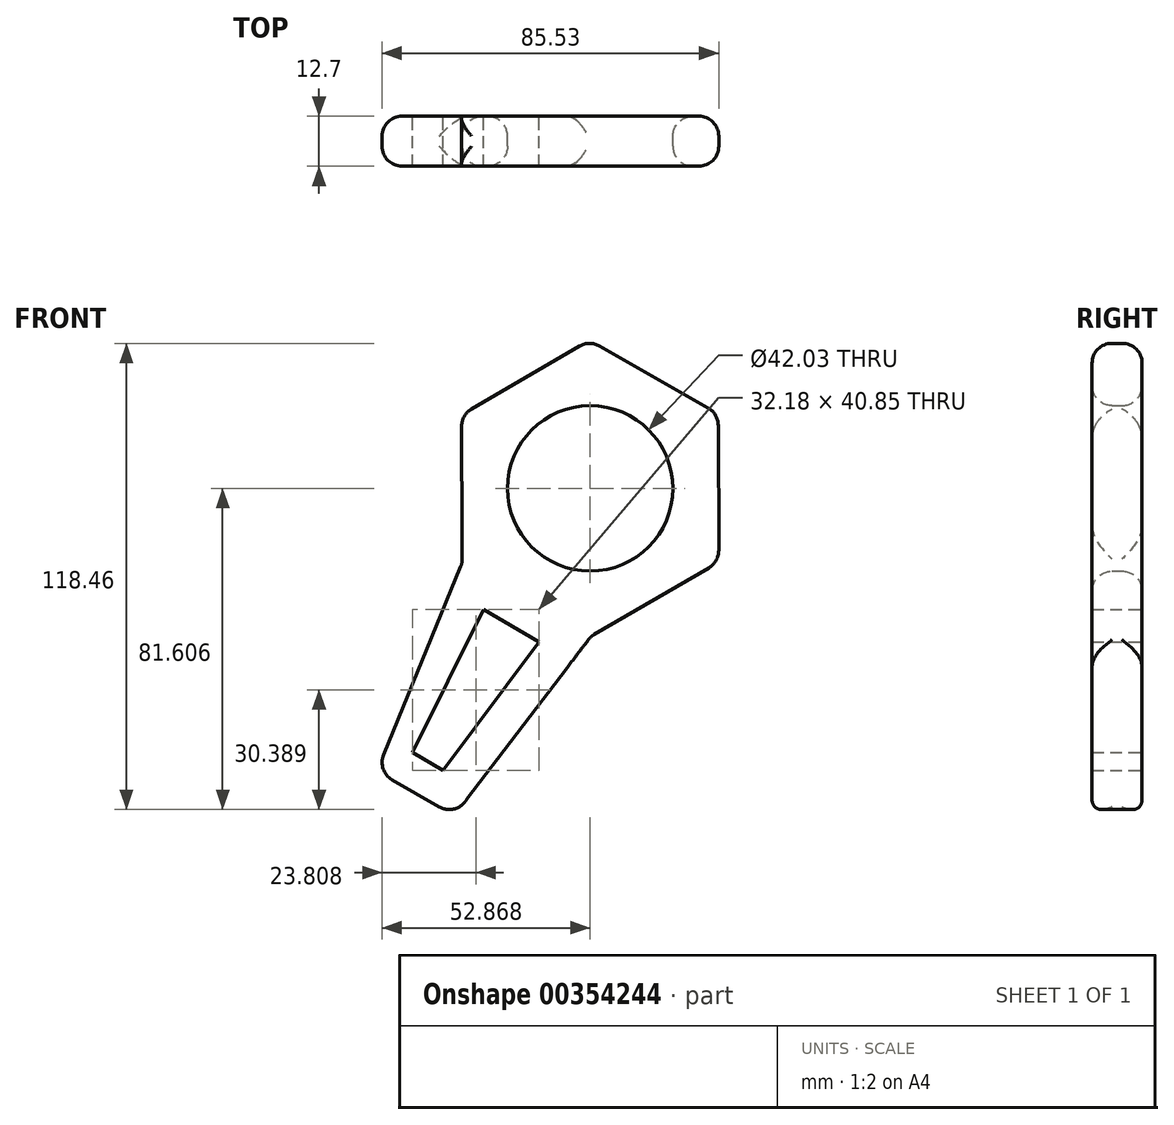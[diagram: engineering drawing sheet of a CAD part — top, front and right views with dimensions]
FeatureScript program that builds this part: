
annotation { "Feature Type Name" : "Feature", "Feature Type Description" : "" }
export const myFeature = defineFeature(function(context is Context, id is Id, definition is map)
    precondition{}
    {
        {
            var Q0;
            Q0=qCreatedBy(makeId("Front.planeOp"),FACE);
            var sketch = newSketch(context, id + "F0", { "sketchPlane" : qUnion([Q0])});
            skCircle(sketch, "E0.MirrorC", {"center": v(0.39, 26.42) * mm, "radius": 32.6 * mm, "construction": true});
            skLineSegment(sketch, "E1.MirrorCS", {"start": v(-32.29, 45.1) * mm, "end": v(-32.13, 7.46) * mm});
            skLineSegment(sketch, "E2.MirrorCS", {"start": v(32.9, 45.37) * mm, "end": v(0.23, 64.06) * mm});
            skLineSegment(sketch, "E3.MirrorCS", {"start": v(0.54, -11.23) * mm, "end": v(33.06, 7.73) * mm});
            skLineSegment(sketch, "E4.MirrorCS", {"start": v(0.23, 64.06) * mm, "end": v(-32.29, 45.1) * mm});
            skLineSegment(sketch, "E5.MirrorCS", {"start": v(33.06, 7.73) * mm, "end": v(32.9, 45.37) * mm});
            skPoint(sketch, "E6.MirrorP", {"position": v(-15.8, -1.88) * mm});
            skLineSegment(sketch, "E7.MirrorCS", {"start": v(-32.13, 7.46) * mm, "end": v(0.54, -11.23) * mm});
            skLineSegment(sketch, "E8.MirrorCS", {"start": v(-32.13, 7.46) * mm, "end": v(-53.79, -45.4) * mm});
            skLineSegment(sketch, "E9.MirrorCS", {"start": v(0.54, -11.23) * mm, "end": v(-34.1, -56.74) * mm});
            skLineSegment(sketch, "E10", {"start": v(-53.79, -45.4) * mm, "end": v(-34.1, -56.74) * mm});
            skCircle(sketch, "E11", {"center": v(0.39, 26.42) * mm, "radius": 21.01 * mm});
            skLineSegment(sketch, "E12", {"start": v(-26.68, -4.38) * mm, "end": v(-12.58, -12.6) * mm});
            skLineSegment(sketch, "E13", {"start": v(-12.58, -12.6) * mm, "end": v(-36.99, -45.23) * mm});
            skLineSegment(sketch, "E14", {"start": v(-36.99, -45.23) * mm, "end": v(-44.76, -40.7) * mm});
            skLineSegment(sketch, "E15", {"start": v(-44.76, -40.7) * mm, "end": v(-26.68, -4.38) * mm});
            skSolve(sketch);
        }
        {
            var Q0;
            Q0=makeQuery(id+"F0.imprint","IMPRINT",FACE,{"disambiguationData":[TD([[makeQuery(id+"F0.imprint","IMPRINT",EDGE,{"derivedFrom":sQuery(id+"F0.wireOp",EDGE,"E1.MirrorCS")}),1.0]])]});
            var Q1;
            Q1=makeQuery(id+"F0.imprint","IMPRINT",FACE,{"disambiguationData":[TD([[makeQuery(id+"F0.imprint","IMPRINT",EDGE,{"derivedFrom":sQuery(id+"F0.wireOp",EDGE,"E7.MirrorCS")}),-1.0]])]});
            extrude(context, id + "F1", {"entities" : qUnion([Q0, Q1]), "depth" : 12.7 * mm});
        }
        {
            var Q0;
            Q0=makeQuery(id+"F1.opExtrude","CAP_EDGE",EDGE,{"disambiguationData":[OSD([sQuery(id+"F0.wireOp",EDGE,"E11")])],"isStart":false});
            var Q1;
            Q1=makeQuery(id+"F1.opExtrude","SWEPT_FACE",FACE,{"disambiguationData":[OSD([sQuery(id+"F0.wireOp",EDGE,"E3.MirrorCS")])]});
            var Q2;
            Q2=makeQuery(id+"F1.opExtrude","SWEPT_FACE",FACE,{"disambiguationData":[OSD([sQuery(id+"F0.wireOp",EDGE,"E5.MirrorCS")])]});
            var Q3;
            Q3=makeQuery(id+"F1.opExtrude","SWEPT_FACE",FACE,{"disambiguationData":[OSD([sQuery(id+"F0.wireOp",EDGE,"E2.MirrorCS")])]});
            var Q4;
            Q4=makeQuery(id+"F1.opExtrude","SWEPT_FACE",FACE,{"disambiguationData":[OSD([sQuery(id+"F0.wireOp",EDGE,"E4.MirrorCS")])]});
            var Q5;
            Q5=makeQuery(id+"F1.opExtrude","SWEPT_FACE",FACE,{"disambiguationData":[OSD([sQuery(id+"F0.wireOp",EDGE,"E8.MirrorCS")])]});
            var Q6;
            Q6=makeQuery(id+"F1.opExtrude","SWEPT_FACE",FACE,{"disambiguationData":[OSD([sQuery(id+"F0.wireOp",EDGE,"E10")])]});
            var Q7;
            Q7=makeQuery(id+"F1.opExtrude","CAP_EDGE",EDGE,{"disambiguationData":[OSD([sQuery(id+"F0.wireOp",EDGE,"E11")])],"isStart":true});
            fillet(context, id + "F2", {"entities" : qUnion([Q0, Q1, Q2, Q3, Q4, Q5, Q6, Q7]), "radius" : 5.08 * mm, "tangentPropagation" : true, "allowEdgeOverflow" : false});
        }
    });
